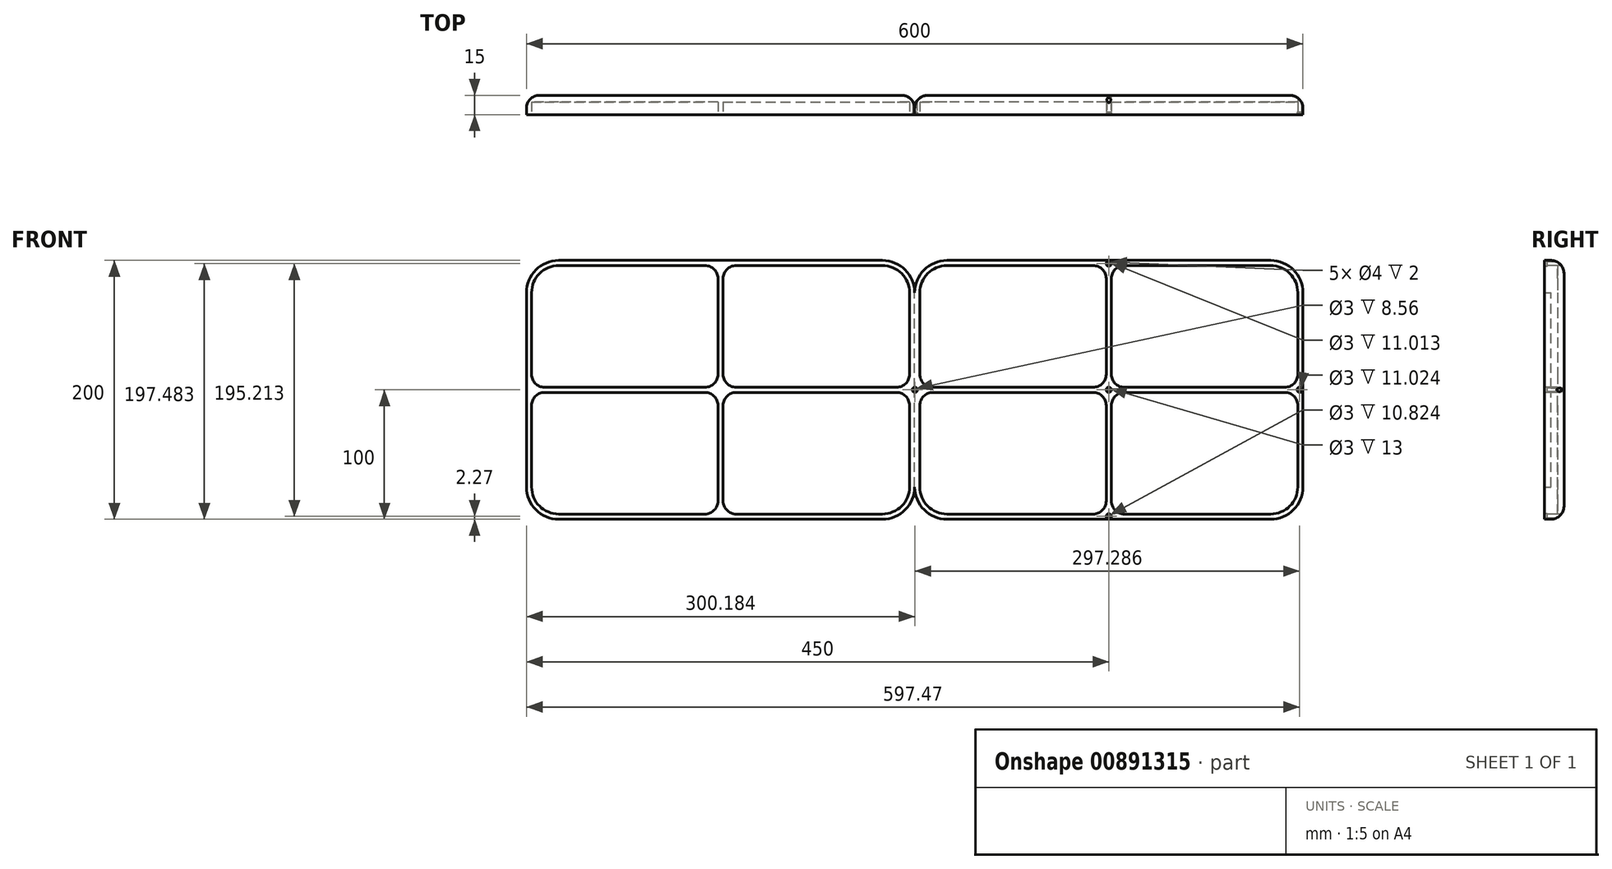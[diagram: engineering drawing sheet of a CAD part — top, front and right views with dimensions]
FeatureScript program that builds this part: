
annotation { "Feature Type Name" : "Feature", "Feature Type Description" : "" }
export const myFeature = defineFeature(function(context is Context, id is Id, definition is map)
    precondition{}
    {
        {
            var Q0;
            Q0=qCreatedBy(makeId("Front.planeOp"),FACE);
            var sketch = newSketch(context, id + "F0", { "sketchPlane" : qUnion([Q0])});
            skLineSegment(sketch, "E0.bottom", {"start": v(125, -100) * mm, "end": v(-125, -100) * mm});
            skLineSegment(sketch, "E0.top", {"start": v(125, 100) * mm, "end": v(-125, 100) * mm});
            skLineSegment(sketch, "E0.left", {"start": v(150, -75) * mm, "end": v(150, 75) * mm});
            skLineSegment(sketch, "E0.right", {"start": v(-150, -75) * mm, "end": v(-150, 75) * mm});
            skPoint(sketch, "E0.middle", {"position": v(0, 0) * mm});
            skPoint(sketch, "E1.visualSharp", {"position": v(-150, 100) * mm});
            skArc(sketch, "E1.filletArc", {"start": v(-125, 100) * mm, "mid": v(-142.68, 92.68) * mm, "end": v(-150, 75) * mm});
            skPoint(sketch, "E2.visualSharp", {"position": v(150, 100) * mm});
            skArc(sketch, "E2.filletArc", {"start": v(150, 75) * mm, "mid": v(142.68, 92.68) * mm, "end": v(125, 100) * mm});
            skPoint(sketch, "E3.visualSharp", {"position": v(150, -100) * mm});
            skArc(sketch, "E3.filletArc", {"start": v(125, -100) * mm, "mid": v(142.68, -92.68) * mm, "end": v(150, -75) * mm});
            skPoint(sketch, "E4.visualSharp", {"position": v(-150, -100) * mm});
            skArc(sketch, "E4.filletArc", {"start": v(-150, -75) * mm, "mid": v(-142.68, -92.68) * mm, "end": v(-125, -100) * mm});
            skSolve(sketch);
        }
        {
            var Q0;
            Q0 = qSketchRegion(id + "F0", true);
            extrude(context, id + "F1", {"entities" : qUnion([Q0]), "depth" : 15 * mm, "offsetDistance" : 25 * mm});
        }
        {
            var Q0;
            Q0=makeQuery(id+"F1.opExtrude","CAP_FACE",FACE,{"disambiguationData":[OSD([sQuery(id+"F0.wireOp",EDGE,"E0.bottom"),sQuery(id+"F0.wireOp",EDGE,"E0.top"),sQuery(id+"F0.wireOp",EDGE,"E0.left"),sQuery(id+"F0.wireOp",EDGE,"E0.right"),sQuery(id+"F0.wireOp",EDGE,"E1.filletArc"),sQuery(id+"F0.wireOp",EDGE,"E2.filletArc"),sQuery(id+"F0.wireOp",EDGE,"E3.filletArc"),sQuery(id+"F0.wireOp",EDGE,"E4.filletArc")])],"isStart":false});
            var sketch = newSketch(context, id + "F2", { "sketchPlane" : qUnion([Q0])});
            skLineSegment(sketch, "E5.0", {"start": v(146, -75) * mm, "end": v(146, -12) * mm});
            skArc(sketch, "E5.1", {"start": v(125, -96) * mm, "mid": v(139.85, -89.85) * mm, "end": v(146, -75) * mm});
            skArc(sketch, "E5.2", {"start": v(146, 75) * mm, "mid": v(139.85, 89.85) * mm, "end": v(125, 96) * mm});
            skLineSegment(sketch, "E5.3", {"start": v(-125, -96) * mm, "end": v(-12, -96) * mm});
            skLineSegment(sketch, "E5.4", {"start": v(125, 96) * mm, "end": v(12, 96) * mm});
            skArc(sketch, "E5.5", {"start": v(-125, 96) * mm, "mid": v(-139.85, 89.85) * mm, "end": v(-146, 75) * mm});
            skLineSegment(sketch, "E5.6", {"start": v(-146, 75) * mm, "end": v(-146, 12) * mm});
            skArc(sketch, "E5.7", {"start": v(-146, -75) * mm, "mid": v(-139.85, -89.85) * mm, "end": v(-125, -96) * mm});
            skLineSegment(sketch, "E6", {"start": v(0, 96) * mm, "end": v(0, -96) * mm, "construction": true});
            skLineSegment(sketch, "E7", {"start": v(146, 0) * mm, "end": v(-146, 0) * mm, "construction": true});
            skLineSegment(sketch, "E8.0", {"start": v(-2, 86) * mm, "end": v(-2, 12) * mm});
            skLineSegment(sketch, "E9.0", {"start": v(136, 2) * mm, "end": v(12, 2) * mm});
            skLineSegment(sketch, "E10.0", {"start": v(2, 86) * mm, "end": v(2, 12) * mm});
            skLineSegment(sketch, "E11.0", {"start": v(136, -2) * mm, "end": v(12, -2) * mm});
            skLineSegment(sketch, "E12.trimOffspring", {"start": v(-12, 96) * mm, "end": v(-125, 96) * mm});
            skLineSegment(sketch, "E13.trimOffspring", {"start": v(-12, 2) * mm, "end": v(-136, 2) * mm});
            skLineSegment(sketch, "E14.trimOffspring", {"start": v(-12, -2) * mm, "end": v(-136, -2) * mm});
            skLineSegment(sketch, "E15.trimOffspring", {"start": v(-2, -12) * mm, "end": v(-2, -86) * mm});
            skLineSegment(sketch, "E16.trimOffspring", {"start": v(2, -12) * mm, "end": v(2, -86) * mm});
            skLineSegment(sketch, "E17.trimOffspring", {"start": v(12, -96) * mm, "end": v(125, -96) * mm});
            skLineSegment(sketch, "E18.trimOffspring", {"start": v(-146, -12) * mm, "end": v(-146, -75) * mm});
            skLineSegment(sketch, "E19.trimOffspring", {"start": v(146, 12) * mm, "end": v(146, 75) * mm});
            skPoint(sketch, "E20.visualSharp", {"position": v(2, 96) * mm});
            skArc(sketch, "E20.filletArc", {"start": v(12, 96) * mm, "mid": v(4.93, 93.07) * mm, "end": v(2, 86) * mm});
            skPoint(sketch, "E21.visualSharp", {"position": v(-2, 96) * mm});
            skArc(sketch, "E21.filletArc", {"start": v(-2, 86) * mm, "mid": v(-4.93, 93.07) * mm, "end": v(-12, 96) * mm});
            skPoint(sketch, "E22.visualSharp", {"position": v(2, 2) * mm});
            skArc(sketch, "E22.filletArc", {"start": v(2, 12) * mm, "mid": v(4.93, 4.93) * mm, "end": v(12, 2) * mm});
            skPoint(sketch, "E23.visualSharp", {"position": v(-2, 2) * mm});
            skArc(sketch, "E23.filletArc", {"start": v(-12, 2) * mm, "mid": v(-4.93, 4.93) * mm, "end": v(-2, 12) * mm});
            skPoint(sketch, "E24.visualSharp", {"position": v(-2, -2) * mm});
            skArc(sketch, "E24.filletArc", {"start": v(-2, -12) * mm, "mid": v(-4.93, -4.93) * mm, "end": v(-12, -2) * mm});
            skPoint(sketch, "E25.visualSharp", {"position": v(2, -2) * mm});
            skArc(sketch, "E25.filletArc", {"start": v(12, -2) * mm, "mid": v(4.93, -4.93) * mm, "end": v(2, -12) * mm});
            skPoint(sketch, "E26.visualSharp", {"position": v(-2, -96) * mm});
            skArc(sketch, "E26.filletArc", {"start": v(-12, -96) * mm, "mid": v(-4.93, -93.07) * mm, "end": v(-2, -86) * mm});
            skPoint(sketch, "E27.visualSharp", {"position": v(2, -96) * mm});
            skArc(sketch, "E27.filletArc", {"start": v(2, -86) * mm, "mid": v(4.93, -93.07) * mm, "end": v(12, -96) * mm});
            skPoint(sketch, "E28.visualSharp", {"position": v(-146, 2) * mm});
            skArc(sketch, "E28.filletArc", {"start": v(-146, 12) * mm, "mid": v(-143.07, 4.93) * mm, "end": v(-136, 2) * mm});
            skPoint(sketch, "E29.visualSharp", {"position": v(-146, -2) * mm});
            skArc(sketch, "E29.filletArc", {"start": v(-136, -2) * mm, "mid": v(-143.07, -4.93) * mm, "end": v(-146, -12) * mm});
            skPoint(sketch, "E30.visualSharp", {"position": v(146, 2) * mm});
            skArc(sketch, "E30.filletArc", {"start": v(136, 2) * mm, "mid": v(143.07, 4.93) * mm, "end": v(146, 12) * mm});
            skPoint(sketch, "E31.visualSharp", {"position": v(146, -2) * mm});
            skArc(sketch, "E31.filletArc", {"start": v(146, -12) * mm, "mid": v(143.07, -4.93) * mm, "end": v(136, -2) * mm});
            skSolve(sketch);
        }
        {
            var Q0;
            Q0=makeQuery(id+"F2.imprint","IMPRINT",FACE,{"disambiguationData":[TD([[makeQuery(id+"F2.imprint","IMPRINT",EDGE,{"derivedFrom":sQuery(id+"F2.wireOp",EDGE,"E5.5")}),1.0]])]});
            var Q1;
            Q1=makeQuery(id+"F2.imprint","IMPRINT",FACE,{"disambiguationData":[TD([[makeQuery(id+"F2.imprint","IMPRINT",EDGE,{"derivedFrom":sQuery(id+"F2.wireOp",EDGE,"E5.2")}),1.0]])]});
            var Q2;
            Q2=makeQuery(id+"F2.imprint","IMPRINT",FACE,{"disambiguationData":[TD([[makeQuery(id+"F2.imprint","IMPRINT",EDGE,{"derivedFrom":sQuery(id+"F2.wireOp",EDGE,"E5.3")}),1.0]])]});
            var Q3;
            Q3=makeQuery(id+"F2.imprint","IMPRINT",FACE,{"disambiguationData":[TD([[makeQuery(id+"F2.imprint","IMPRINT",EDGE,{"derivedFrom":sQuery(id+"F2.wireOp",EDGE,"E5.0")}),1.0]])]});
            extrude(context, id + "F3", {"entities" : qUnion([Q0, Q1, Q2, Q3]), "operationType" : NewBodyOperationType.REMOVE, "oppositeDirection" : true, "depth" : 10 * mm, "offsetDistance" : 25 * mm});
        }
        {
            var Q0;
            Q0=makeQuery(id+"F1.opExtrude","CAP_EDGE",EDGE,{"disambiguationData":[OSD([sQuery(id+"F0.wireOp",EDGE,"E0.top")])],"isStart":true});
            fillet(context, id + "F4", {"entities" : qUnion([Q0]), "radius" : 10 * mm, "tangentPropagation" : true, "allowEdgeOverflow" : false});
        }
        {
            var Q0;
            Q0=makeQuery(id+"F1.opExtrude","SWEPT_FACE",FACE,{"disambiguationData":[OSD([sQuery(id+"F0.wireOp",EDGE,"E0.right")])]});
            cPlane(context, id + "F5", {"entities" : qUnion([Q0]), "cplaneType" : CPlaneType.OFFSET, "offset" : 0 * mm, "width" : 150 * mm, "height" : 150 * mm});
        }
        {
            var Q0;
            Q0=makeQuery(id+"F1.opExtrude","SWEPT_BODY",BODY,{"disambiguationData":[OSD([sQuery(id+"F0.wireOp",EDGE,"E0.bottom"),sQuery(id+"F0.wireOp",EDGE,"E0.top"),sQuery(id+"F0.wireOp",EDGE,"E0.left"),sQuery(id+"F0.wireOp",EDGE,"E0.right"),sQuery(id+"F0.wireOp",EDGE,"E1.filletArc"),sQuery(id+"F0.wireOp",EDGE,"E2.filletArc"),sQuery(id+"F0.wireOp",EDGE,"E3.filletArc"),sQuery(id+"F0.wireOp",EDGE,"E4.filletArc")])]});
            var Q1;
            Q1=qCreatedBy(id+"F5.planeOp",FACE);
            mirror(context, id + "F6", {"operationType" : NewBodyOperationType.ADD, "entities" : qUnion([Q0]), "mirrorPlane" : qUnion([Q1])});
        }
        {
            var Q0;
            {var subQ0=makeQuery(id+"F1.opExtrude","CAP_FACE",FACE,{"disambiguationData":[OSD([sQuery(id+"F0.wireOp",EDGE,"E0.bottom"),sQuery(id+"F0.wireOp",EDGE,"E0.top"),sQuery(id+"F0.wireOp",EDGE,"E0.left"),sQuery(id+"F0.wireOp",EDGE,"E0.right"),sQuery(id+"F0.wireOp",EDGE,"E1.filletArc"),sQuery(id+"F0.wireOp",EDGE,"E2.filletArc"),sQuery(id+"F0.wireOp",EDGE,"E3.filletArc"),sQuery(id+"F0.wireOp",EDGE,"E4.filletArc")])],"isStart":false});Q0=makeQuery(id+"F6.boolean.opBoolean","MERGE",FACE,{"derivedFrom":[subQ0,makeQuery(id+"F6.opPattern","COPY",FACE,{"derivedFrom":subQ0,"instanceName":"1"})]});}
            var sketch = newSketch(context, id + "F7", { "sketchPlane" : qUnion([Q0])});
            skSolve(sketch);
        }
        {
            var Q0;
            {var subQ6=makeQuery(id+"F1.opExtrude","CAP_EDGE",EDGE,{"disambiguationData":[OSD([sQuery(id+"F0.wireOp",EDGE,"E0.bottom")])],"isStart":false});Q0=makeQuery(id+"F7.imprint","IMPRINT",FACE,{"disambiguationData":[TD([[makeQuery(id+"F7.imprint","IMPRINT",EDGE,{"derivedFrom":subQ6}),-1.0]])]});}
            var sketch = newSketch(context, id + "F8", { "sketchPlane" : qUnion([Q0])});
            skPoint(sketch, "E32", {"position": v(0, 0) * mm});
            skPoint(sketch, "E33", {"position": v(0, -97.73) * mm});
            skPoint(sketch, "E34", {"position": v(0, 97.48) * mm});
            skPoint(sketch, "E35", {"position": v(147.47, 0) * mm});
            skPoint(sketch, "E36", {"position": v(-149.82, 0) * mm});
            skSolve(sketch);
        }
        {
            var Q0;
            Q0=sQuery(id+"F8.wireOp",VERTEX,"E32");
            var Q1;
            Q1=sQuery(id+"F8.wireOp",VERTEX,"E33");
            var Q2;
            Q2=sQuery(id+"F8.wireOp",VERTEX,"E36");
            var Q3;
            Q3=sQuery(id+"F8.wireOp",VERTEX,"E34");
            var Q4;
            Q4=sQuery(id+"F8.wireOp",VERTEX,"E35");
            var Q5;
            Q5=makeQuery(id+"F1.opExtrude","SWEPT_BODY",BODY,{"disambiguationData":[OSD([sQuery(id+"F0.wireOp",EDGE,"E0.bottom"),sQuery(id+"F0.wireOp",EDGE,"E0.top"),sQuery(id+"F0.wireOp",EDGE,"E0.left"),sQuery(id+"F0.wireOp",EDGE,"E0.right"),sQuery(id+"F0.wireOp",EDGE,"E1.filletArc"),sQuery(id+"F0.wireOp",EDGE,"E2.filletArc"),sQuery(id+"F0.wireOp",EDGE,"E3.filletArc"),sQuery(id+"F0.wireOp",EDGE,"E4.filletArc")])]});
            hole(context, id + "F9", {"style" : HoleStyle.C_BORE, "endStyle" : HoleEndStyle.THROUGH, "holeDiameter" : 3 * mm, "cBoreDiameter" : 4 * mm, "cBoreDepth" : 2 * mm, "majorDiameter" : 5 * mm, "isTappedThrough" : true, "tappedDepth" : 12 * mm, "tapClearance" : 3, "locations" : qUnion([Q0, Q1, Q2, Q3, Q4]), "scope" : qUnion([Q5])});
        }
    });
